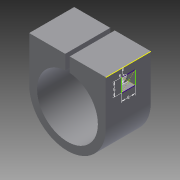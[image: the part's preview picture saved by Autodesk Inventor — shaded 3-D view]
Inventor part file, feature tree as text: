
AUTODESK INVENTOR PART (.ipt)
format: ipt  version: 2013 (Build 170138000, 138)  size: 113,664 bytes
history: native  units: mm
features: extrude x2, sketch x2, hole x1
ambient origin geometry x8: Origin, YZ Plane, XZ Plane, XY Plane, X Axis, Y Axis, Z Axis, Center Point
bodies: Solid1 (feature_tree)
feature tree (5):
  extrude  "Extrusion1"  Depth=34.0mm
  sketch  "Sketch2"  dims[d5=20.0mm d6=0.0mm d7=6.52mm d8=5.791mm d9=6.0mm d10=12.6mm d11=2.0mm d12=90.0deg d13=8.0mm d14=20.594885mm d15=6.0mm d16=6.0mm d17=3.3mm d18=0.0mm]
  hole  "Hole1"  [1 undecoded]
  extrude  "Extrusion2"  Depth=6.0mm
  sketch  "Sketch1"  dims[d0=27.0mm d1=34.0mm]
note: 1 required parameter value undecoded (feature->parameter linkage not recoverable at this tier; creation-order binding heuristic only, values carry confidence <= 0.55)
